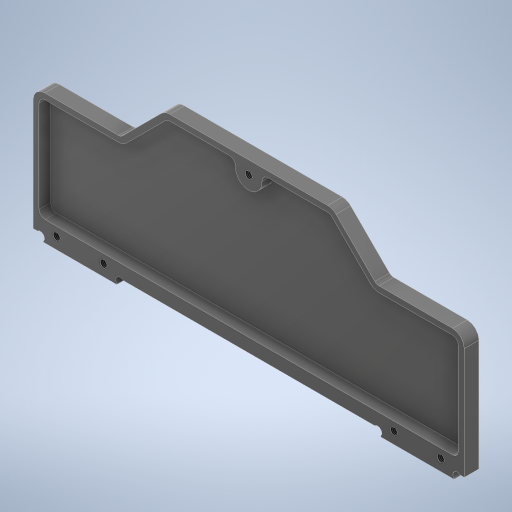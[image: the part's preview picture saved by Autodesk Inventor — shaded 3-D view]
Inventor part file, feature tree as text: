
AUTODESK INVENTOR PART (.ipt)
format: ipt  version: 2024.2 (Build 282272000, 272)  size: 395,776 bytes
history: native  units: mm
features: extrude x2, sketch x1
ambient origin geometry x8: Origin, YZ Plane, XZ Plane, XY Plane, X Axis, Y Axis, Z Axis, Center Point
bodies: Solid1 (feature_tree)
feature tree (3):
  sketch  "Sketch1"  dims[d0=147.0mm d2=16.0mm d3=3.9mm d4=25.0mm d5=7.9mm d6=5.0mm d7=0.0mm d8=2.459mm d9=6.0mm d10=4.0mm d11=2.0mm d12=90.0deg d13=8.8mm d14=0.0mm d18=5.0mm d28=1.0mm d35=2.1mm d36=0.5mm d37=95.200425mm d38=115.0mm d45=2.0mm d46=2.0mm d47=2.0mm d50=6.0mm d51=4.0mm d52=0.0mm d53=2.0mm d55=4.0mm d56=1.5mm d57=42.5mm d59=1.0mm d60=14.0mm d63=45.0deg d64=15.0mm d65=1.0mm d66=1.0mm d67=88.0mm d68=43.5mm d69=4.5mm d70=2.0mm d71=2.0mm d41=0.0mm d42=0.0mm d43=0.0mm d44=0.0mm]
  extrude  "Extrusion1"  Depth=2.0mm
  extrude  "Extrusion2"  Depth=2.0mm
